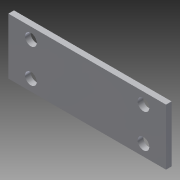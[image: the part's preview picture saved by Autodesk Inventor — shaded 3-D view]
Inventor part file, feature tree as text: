
AUTODESK INVENTOR PART (.ipt)
format: ipt  version: 2013 (Build 170138000, 138)  size: 86,528 bytes
history: native  units: in
note: dims shown in document units (in); Inventor stores cm internally (conversion verified against a paired STEP export)
features: extrude x1, sketch x1
ambient origin geometry x8: Origin, YZ Plane, XZ Plane, XY Plane, X Axis, Y Axis, Z Axis, Center Point
bodies: Solid1 (feature_tree)
feature tree (2):
  extrude  "Extrusion1"  Depth=1.25in
  sketch  "Sketch1"  dims[d0=3.5in d2=1.25in d3=0.7874in d5=2.5in d6=0.7874in d8=0.75in d11=0.25in d12=0.26in d13=0.125in d14=0.0in]
